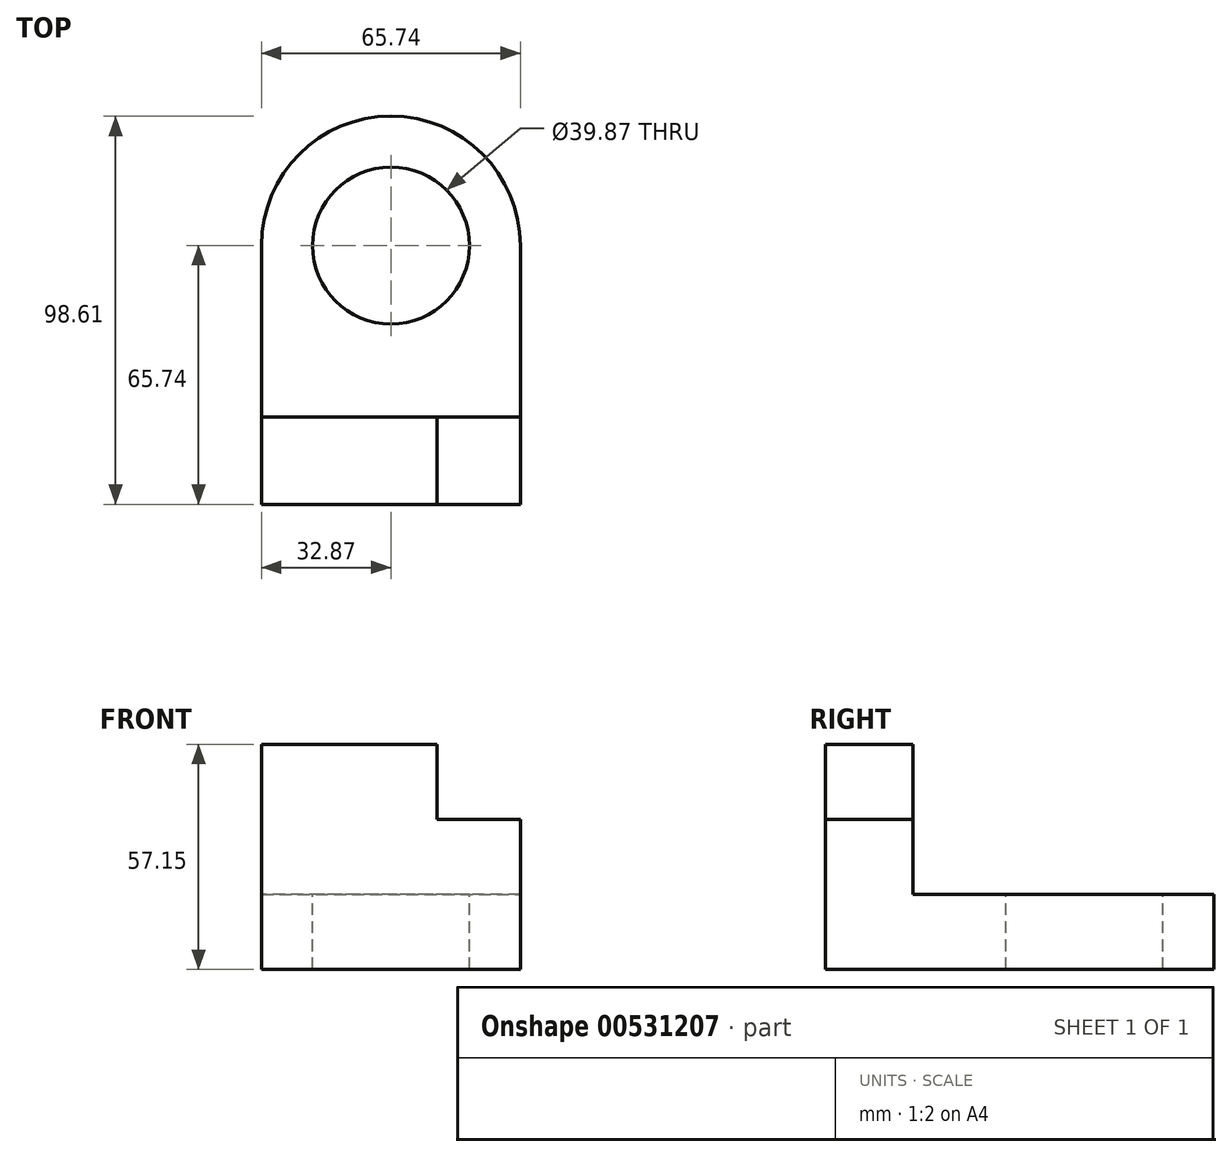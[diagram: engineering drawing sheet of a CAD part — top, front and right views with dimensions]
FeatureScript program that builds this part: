
annotation { "Feature Type Name" : "Feature", "Feature Type Description" : "" }
export const myFeature = defineFeature(function(context is Context, id is Id, definition is map)
    precondition{}
    {
        {
            var Q0;
            Q0=qCreatedBy(makeId("Top.planeOp"),FACE);
            var sketch = newSketch(context, id + "F0", { "sketchPlane" : qUnion([Q0])});
            skLineSegment(sketch, "E0.bottom", {"start": v(-32.87, 32.87) * mm, "end": v(32.87, 32.87) * mm});
            skLineSegment(sketch, "E0.top", {"start": v(-32.87, -32.87) * mm, "end": v(32.87, -32.87) * mm});
            skLineSegment(sketch, "E0.left", {"start": v(-32.87, 32.87) * mm, "end": v(-32.87, -32.87) * mm});
            skLineSegment(sketch, "E0.right", {"start": v(32.87, 32.87) * mm, "end": v(32.87, -32.87) * mm});
            skPoint(sketch, "E0.middle", {"position": v(0, 0) * mm});
            skCircle(sketch, "E1", {"center": v(0, 32.87) * mm, "radius": 32.87 * mm});
            skSolve(sketch);
        }
        {
            var Q0;
            Q0 = qSketchRegion(id + "F0", true);
            extrude(context, id + "F1", {"entities" : qUnion([Q0]), "depth" : 19.05 * mm, "offsetDistance" : 25.4 * mm});
        }
        {
            var Q0;
            Q0=makeQuery(id+"F1.opExtrude","CAP_FACE",FACE,{"disambiguationData":[OSD([sQuery(id+"F0.wireOp",EDGE,"E0.top"),sQuery(id+"F0.wireOp",EDGE,"E0.left"),sQuery(id+"F0.wireOp",EDGE,"E0.right"),sQuery(id+"F0.wireOp",EDGE,"E1")])],"isStart":false});
            var sketch = newSketch(context, id + "F2", { "sketchPlane" : qUnion([Q0])});
            skLineSegment(sketch, "E2.bottom", {"start": v(-32.87, -32.87) * mm, "end": v(11.72, -32.87) * mm});
            skLineSegment(sketch, "E2.top", {"start": v(-32.87, -10.7) * mm, "end": v(11.72, -10.7) * mm});
            skLineSegment(sketch, "E2.left", {"start": v(-32.87, -32.87) * mm, "end": v(-32.87, -10.7) * mm});
            skLineSegment(sketch, "E2.right", {"start": v(11.72, -32.87) * mm, "end": v(11.72, -10.7) * mm});
            skLineSegment(sketch, "E3.bottom", {"start": v(11.72, -10.7) * mm, "end": v(32.87, -10.7) * mm});
            skLineSegment(sketch, "E3.top", {"start": v(11.72, -32.87) * mm, "end": v(32.87, -32.87) * mm});
            skLineSegment(sketch, "E3.left", {"start": v(11.72, -10.7) * mm, "end": v(11.72, -32.87) * mm});
            skLineSegment(sketch, "E3.right", {"start": v(32.87, -10.7) * mm, "end": v(32.87, -32.87) * mm});
            skSolve(sketch);
        }
        {
            var Q0;
            Q0=makeQuery(id+"F2.imprint","IMPRINT",FACE,{"disambiguationData":[TD([[makeQuery(id+"F2.imprint","IMPRINT",EDGE,{"derivedFrom":sQuery(id+"F2.wireOp",EDGE,"E2.bottom")}),1.0]])]});
            extrude(context, id + "F3", {"entities" : qUnion([Q0]), "operationType" : NewBodyOperationType.ADD, "depth" : 38.1 * mm, "offsetDistance" : 25.4 * mm});
        }
        {
            var Q0;
            Q0=makeQuery(id+"F1.opExtrude","CAP_FACE",FACE,{"disambiguationData":[OSD([sQuery(id+"F0.wireOp",EDGE,"E0.top"),sQuery(id+"F0.wireOp",EDGE,"E0.left"),sQuery(id+"F0.wireOp",EDGE,"E0.right"),sQuery(id+"F0.wireOp",EDGE,"E1")])],"isStart":false});
            var sketch = newSketch(context, id + "F4", { "sketchPlane" : qUnion([Q0])});
            skLineSegment(sketch, "E4.bottom", {"start": v(32.87, -32.87) * mm, "end": v(11.72, -32.87) * mm});
            skLineSegment(sketch, "E4.top", {"start": v(32.87, -10.7) * mm, "end": v(11.72, -10.7) * mm});
            skLineSegment(sketch, "E4.left", {"start": v(32.87, -32.87) * mm, "end": v(32.87, -10.7) * mm});
            skLineSegment(sketch, "E4.right", {"start": v(11.72, -32.87) * mm, "end": v(11.72, -10.7) * mm});
            skSolve(sketch);
        }
        {
            var Q0;
            Q0=makeQuery(id+"F4.imprint","IMPRINT",FACE,{"disambiguationData":[TD([[makeQuery(id+"F4.imprint","IMPRINT",EDGE,{"derivedFrom":sQuery(id+"F4.wireOp",EDGE,"E4.bottom")}),1.0]])]});
            extrude(context, id + "F5", {"entities" : qUnion([Q0]), "operationType" : NewBodyOperationType.ADD, "depth" : 19.05 * mm, "offsetDistance" : 25.4 * mm});
        }
        {
            var Q0;
            Q0=makeQuery(id+"F1.opExtrude","CAP_FACE",FACE,{"disambiguationData":[OSD([sQuery(id+"F0.wireOp",EDGE,"E0.top"),sQuery(id+"F0.wireOp",EDGE,"E0.left"),sQuery(id+"F0.wireOp",EDGE,"E0.right"),sQuery(id+"F0.wireOp",EDGE,"E1")])],"isStart":false});
            var sketch = newSketch(context, id + "F6", { "sketchPlane" : qUnion([Q0])});
            skCircle(sketch, "E5", {"center": v(0, 32.87) * mm, "radius": 19.94 * mm});
            skSolve(sketch);
        }
        {
            var Q0;
            Q0 = qSketchRegion(id + "F6", true);
            extrude(context, id + "F7", {"entities" : qUnion([Q0]), "operationType" : NewBodyOperationType.REMOVE, "oppositeDirection" : true, "depth" : 25.4 * mm, "offsetDistance" : 25.4 * mm});
        }
    });
